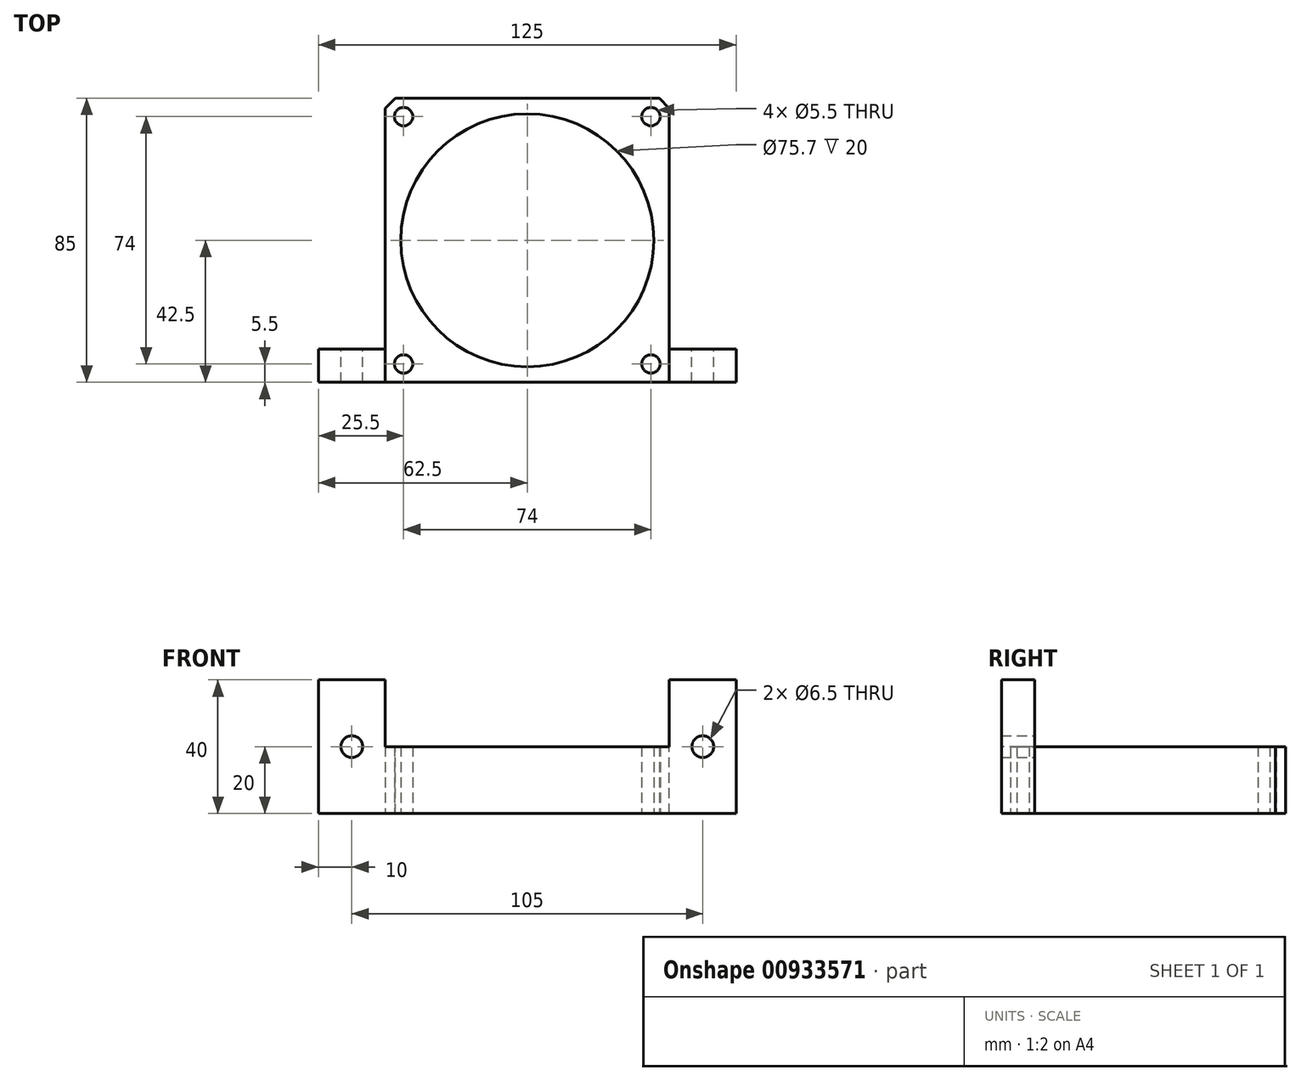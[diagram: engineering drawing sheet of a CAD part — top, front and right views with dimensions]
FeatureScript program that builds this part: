
annotation { "Feature Type Name" : "Feature", "Feature Type Description" : "" }
export const myFeature = defineFeature(function(context is Context, id is Id, definition is map)
    precondition{}
    {
        {
            var Q0;
            Q0=qCreatedBy(makeId("Top.planeOp"),FACE);
            var sketch = newSketch(context, id + "F0", { "sketchPlane" : qUnion([Q0])});
            skLineSegment(sketch, "E0.bottom", {"start": v(42.5, 42.5) * mm, "end": v(-42.5, 42.5) * mm});
            skLineSegment(sketch, "E0.top", {"start": v(42.5, -42.5) * mm, "end": v(-42.5, -42.5) * mm});
            skLineSegment(sketch, "E0.left", {"start": v(42.5, 42.5) * mm, "end": v(42.5, -42.5) * mm});
            skLineSegment(sketch, "E0.right", {"start": v(-42.5, 42.5) * mm, "end": v(-42.5, -42.5) * mm});
            skPoint(sketch, "E0.middle", {"position": v(0, 0) * mm});
            skCircle(sketch, "E1", {"center": v(0, 0) * mm, "radius": 37.85 * mm});
            skCircle(sketch, "E2", {"center": v(37, 37) * mm, "radius": 2.75 * mm});
            skCircle(sketch, "E3.MirrorC", {"center": v(-37, 37) * mm, "radius": 2.75 * mm});
            skCircle(sketch, "E4.MirrorC", {"center": v(-37, -37) * mm, "radius": 2.75 * mm});
            skCircle(sketch, "E5.MirrorC", {"center": v(37, -37) * mm, "radius": 2.75 * mm});
            skSolve(sketch);
        }
        {
            var Q0;
            Q0 = qSketchRegion(id + "F0", true);
            extrude(context, id + "F1", {"entities" : qUnion([Q0]), "depth" : 20 * mm, "offsetDistance" : 25 * mm});
        }
        {
            var Q0;
            Q0=qCreatedBy(makeId("Top.planeOp"),FACE);
            var sketch = newSketch(context, id + "F2", { "sketchPlane" : qUnion([Q0])});
            skLineSegment(sketch, "E6.bottom", {"start": v(-42.5, -32.5) * mm, "end": v(-62.5, -32.5) * mm});
            skLineSegment(sketch, "E6.top", {"start": v(-42.5, -42.5) * mm, "end": v(-62.5, -42.5) * mm});
            skLineSegment(sketch, "E6.left", {"start": v(-42.5, -32.5) * mm, "end": v(-42.5, -42.5) * mm});
            skLineSegment(sketch, "E6.right", {"start": v(-62.5, -32.5) * mm, "end": v(-62.5, -42.5) * mm});
            skLineSegment(sketch, "E7.MirrorCS", {"start": v(42.5, -32.5) * mm, "end": v(62.5, -32.5) * mm});
            skLineSegment(sketch, "E8.MirrorCS", {"start": v(42.5, -42.5) * mm, "end": v(62.5, -42.5) * mm});
            skLineSegment(sketch, "E9.MirrorCS", {"start": v(62.5, -32.5) * mm, "end": v(62.5, -42.5) * mm});
            skLineSegment(sketch, "E10.MirrorCS", {"start": v(42.5, -32.5) * mm, "end": v(42.5, -42.5) * mm});
            skSolve(sketch);
        }
        {
            var Q0;
            Q0 = qSketchRegion(id + "F2", true);
            extrude(context, id + "F3", {"entities" : qUnion([Q0]), "operationType" : NewBodyOperationType.ADD, "depth" : 40 * mm, "offsetDistance" : 25 * mm});
        }
        {
            var Q0;
            Q0=makeQuery(id+"F3.opExtrude","SWEPT_FACE",FACE,{"disambiguationData":[OSD([sQuery(id+"F2.wireOp",EDGE,"E7.MirrorCS")])]});
            var sketch = newSketch(context, id + "F4", { "sketchPlane" : qUnion([Q0])});
            skCircle(sketch, "E11", {"center": v(-52.5, 20) * mm, "radius": 3.25 * mm});
            skCircle(sketch, "E12.MirrorC", {"center": v(52.5, 20) * mm, "radius": 3.25 * mm});
            skSolve(sketch);
        }
        {
            var Q0;
            Q0 = qSketchRegion(id + "F4", true);
            extrude(context, id + "F5", {"entities" : qUnion([Q0]), "operationType" : NewBodyOperationType.REMOVE, "endBound" : BoundingType.THROUGH_ALL, "oppositeDirection" : true, "depth" : 25 * mm, "offsetDistance" : 25 * mm});
        }
        {
            var Q0;
            Q0=makeQuery(id+"F1.opExtrude","SWEPT_EDGE",EDGE,{"disambiguationData":[OSD([sQuery(id+"F0.wireOp",EDGE,"E0.bottom"),sQuery(id+"F0.wireOp",EDGE,"E0.right")])]});
            var Q1;
            Q1=makeQuery(id+"F1.opExtrude","SWEPT_EDGE",EDGE,{"disambiguationData":[OSD([sQuery(id+"F0.wireOp",EDGE,"E0.bottom"),sQuery(id+"F0.wireOp",EDGE,"E0.left")])]});
            chamfer(context, id + "F6", {"entities" : qUnion([Q0, Q1]), "width" : 3 * mm, "tangentPropagation" : true});
        }
    });
